MODEL slx_53ea6de5a571
CONFIG AbsTol = auto
CONFIG FixedStep = auto
CONFIG MaxStep = auto
CONFIG MinStep = auto
CONFIG RelTol = 1e-3
CONFIG SampleTimeConstraint = Unconstrained
CONFIG Solver = ode45
CONFIG SolverMode = Auto
CONFIG SolverName = ode45
CONFIG StartTime = 0.0
CONFIG StopTime = 10.0
BLOCK [Gain] D_a
  Gain = 0.0143
  OutDataTypeStr = Inherit: Inherit via internal rule
  ParamDataTypeStr = Inherit: Inherit via internal rule
  SaturateOnIntegerOverflow = off
BLOCK [Gain] D_error
  Gain = 0.05
  OutDataTypeStr = Inherit: Inherit via internal rule
  ParamDataTypeStr = Inherit: Inherit via internal rule
  SaturateOnIntegerOverflow = off
BLOCK [Derivative] Derivative
  CoefficientInTFapproximation = 1000000
BLOCK [Derivative] Derivative1
  CoefficientInTFapproximation = 1000000
BLOCK [Gain] Gear
  Gain = 6
  OutDataTypeStr = Inherit: Inherit via internal rule
  ParamDataTypeStr = Inherit: Inherit via internal rule
  SaturateOnIntegerOverflow = off
BLOCK [Gain] Gear2
  OutDataTypeStr = Inherit: Inherit via internal rule
  ParamDataTypeStr = Inherit: Inherit via internal rule
  SaturateOnIntegerOverflow = off
BLOCK [Gain] Gear3
  Gain = 6
  OutDataTypeStr = Inherit: Inherit via internal rule
  ParamDataTypeStr = Inherit: Inherit via internal rule
  SaturateOnIntegerOverflow = off
BLOCK [Gain] J_a
  Gain = 542E-7
  OutDataTypeStr = Inherit: Inherit via internal rule
  ParamDataTypeStr = Inherit: Inherit via internal rule
  SaturateOnIntegerOverflow = off
BLOCK [Gain] J_error
  Gain = 0.000001
  OutDataTypeStr = Inherit: Inherit via internal rule
  ParamDataTypeStr = Inherit: Inherit via internal rule
  SaturateOnIntegerOverflow = off
BLOCK [Gain] Kb
  Gain = 0.038506
  OutDataTypeStr = Inherit: Inherit via internal rule
  ParamDataTypeStr = Inherit: Inherit via internal rule
  SaturateOnIntegerOverflow = off
BLOCK [Gain] Kt
  Gain = 0.0385
  OutDataTypeStr = Inherit: Inherit via internal rule
  ParamDataTypeStr = Inherit: Inherit via internal rule
  SaturateOnIntegerOverflow = off
BLOCK [TransferFcn] Motor tidskonstant
  Denominator = [1 0.00378^-1]
  Numerator = [0.00378^-1]
BLOCK [Outport] Out1
  IconDisplay = Port number
BLOCK [Outport] Out2
  IconDisplay = Port number
  Port = 2
BLOCK [Reference] PID Controller  REF=simulink/Continuous/PID Controller
  AntiWindupMode = clamping
  Controller = PI
  ControllerParametersSource = internal
  D = 0
  DGainOutDataTypeStr = Inherit: Inherit via internal rule
  DOutDataTypeStr = Inherit: Inherit via internal rule
  DOutMax = []
  DOutMin = []
  DParamDataTypeStr = Inherit: Inherit via internal rule
  DParamMax = []
  DParamMin = []
  DProdOutDataTypeStr = Inherit: Inherit via internal rule
  DifferentiatorICPrevScaledInput = 0
  DifferentiatorOutDataTypeStr = Inherit: Inherit via internal rule
  DifferentiatorOutMax = []
  DifferentiatorOutMin = []
  ExternalReset = none
  FilterContinuousStateAttributes = ''
  FilterMethod = Forward Euler
  FilterOutDataTypeStr = Inherit: Inherit via internal rule
  FilterOutMax = []
  FilterOutMin = []
  FilterRTWStateStorageClass = Auto
  FilterStateMustResolveToSignalObject = off
  Form = Parallel
  I = 6000
  IGainOutDataTypeStr = Inherit: Inherit via internal rule
  IOutDataTypeStr = Inherit: Inherit via internal rule
  IOutMax = []
  IOutMin = []
  IParamDataTypeStr = Inherit: Inherit via internal rule
  IParamMax = []
  IParamMin = []
  IProdOutDataTypeStr = Inherit: Inherit via internal rule
  IgnoreLimit = off
  InitialConditionForFilter = 0
  InitialConditionForIntegrator = 0
  InitialConditionSource = internal
  IntegratorContinuousStateAttributes = ''
  IntegratorMethod = Forward Euler
  IntegratorOutDataTypeStr = Inherit: Inherit via internal rule
  IntegratorOutMax = []
  IntegratorOutMin = []
  IntegratorRTWStateStorageClass = Auto
  IntegratorStateMustResolveToSignalObject = off
  Kb = 1
  KbOutDataTypeStr = Inherit: Inherit via internal rule
  KbOutMax = []
  KbOutMin = []
  KbParamDataTypeStr = Inherit: Inherit via internal rule
  KbParamMax = []
  KbParamMin = []
  Kt = 1
  KtOutDataTypeStr = Inherit: Inherit via internal rule
  KtOutMax = []
  KtOutMin = []
  KtParamDataTypeStr = Inherit: Inherit via internal rule
  KtParamMax = []
  KtParamMin = []
  LimitOutput = on
  LinearizeAsGain = off
  LockScale = off
  LowerSaturationLimit = 0
  N = 100
  NGainOutDataTypeStr = Inherit: Inherit via internal rule
  NOutDataTypeStr = Inherit: Inherit via internal rule
  NOutMax = []
  NOutMin = []
  NParamDataTypeStr = Inherit: Inherit via internal rule
  NParamMax = []
  NParamMin = []
  NProdOutDataTypeStr = Inherit: Inherit via internal rule
  P = 5
  PGainOutDataTypeStr = Inherit: Inherit via internal rule
  POutDataTypeStr = Inherit: Inherit via internal rule
  POutMax = []
  POutMin = []
  PParamDataTypeStr = Inherit: Inherit via internal rule
  PParamMax = []
  PParamMin = []
  PProdOutDataTypeStr = Inherit: Inherit via internal rule
  Ports = [1, 1]
  RndMeth = Floor
  SampleTime = -1
  SaturateOnIntegerOverflow = off
  SaturationOutDataTypeStr = Inherit: Same as input
  SaturationOutMax = []
  SaturationOutMin = []
  SourceBlock = simulink/Continuous/PID Controller
  SourceType = PID 1dof
  SumAccumDataTypeStr = Inherit: Inherit via internal rule
  SumDAccumDataTypeStr = Inherit: Inherit via internal rule
  SumDOutDataTypeStr = Inherit: Inherit via internal rule
  SumDOutMax = []
  SumDOutMin = []
  SumI1AccumDataTypeStr = Inherit: Inherit via internal rule
  SumI1OutDataTypeStr = Inherit: Inherit via internal rule
  SumI1OutMax = []
  SumI1OutMin = []
  SumI2AccumDataTypeStr = Inherit: Inherit via internal rule
  SumI2OutDataTypeStr = Inherit: Inherit via internal rule
  SumI2OutMax = []
  SumI2OutMin = []
  SumI3AccumDataTypeStr = Inherit: Inherit via internal rule
  SumI3OutDataTypeStr = Inherit: Inherit via internal rule
  SumI3OutMax = []
  SumI3OutMin = []
  SumOutDataTypeStr = Inherit: Inherit via internal rule
  SumOutMax = []
  SumOutMin = []
  TimeDomain = Continuous-time
  TrackingMode = off
  UpperSaturationLimit = 100
  UseFilter = off
  ZeroCross = on
BLOCK [Gain] PWM->Volt
  Gain = 1/100
  OutDataTypeStr = Inherit: Inherit via internal rule
  ParamDataTypeStr = Inherit: Inherit via internal rule
  SaturateOnIntegerOverflow = off
BLOCK [Product] Product
  InputSameDT = off
  OutDataTypeStr = Inherit: Inherit via internal rule
  Ports = [2, 1]
  RndMeth = Floor
  SaturateOnIntegerOverflow = off
BLOCK [Quantizer] Quantizer
BLOCK [RateLimiter] Rate Limiter
  RisingSlewLimit = 5
BLOCK [Step] Step Hastighed
  After = 30
  SampleTime = 0
BLOCK [Sum] Sum
  IconShape = round
  InputSameDT = off
  Inputs = |+-
  OutDataTypeStr = Inherit: Inherit via internal rule
  Ports = [2, 1]
  SaturateOnIntegerOverflow = off
BLOCK [Sum] Sum1
  IconShape = round
  InputSameDT = off
  Inputs = ++|
  OutDataTypeStr = Inherit: Inherit via internal rule
  Ports = [2, 1]
  SaturateOnIntegerOverflow = off
BLOCK [Sum] Sum2
  IconShape = round
  InputSameDT = off
  Inputs = +|+
  OutDataTypeStr = Inherit: Inherit via internal rule
  Ports = [2, 1]
  SaturateOnIntegerOverflow = off
BLOCK [Sum] Sum3
  IconShape = round
  InputSameDT = off
  Inputs = +|+
  OutDataTypeStr = Inherit: Inherit via internal rule
  Ports = [2, 1]
  SaturateOnIntegerOverflow = off
BLOCK [Sum] Sum4
  IconShape = round
  InputSameDT = off
  Inputs = ++|
  OutDataTypeStr = Inherit: Inherit via internal rule
  Ports = [2, 1]
  SaturateOnIntegerOverflow = off
BLOCK [TransferFcn] Transfer Fcn
  Denominator = [0.000072 0.608]
BLOCK [TransferFcn] Transfer Fcn1
  Denominator = [1 5]
  Numerator = [5]
BLOCK [UnitDelay] Unit Delay
  InputProcessing = Elements as channels (sample based)
  SampleTime = 0.005
BLOCK [UnitDelay] Unit Delay1
  InputProcessing = Elements as channels (sample based)
  SampleTime = 0.005
BLOCK [Constant] set Moment
  Value = 1.6
BLOCK [Constant] set Moment1
  Value = 30
BLOCK [Gain] v->omega
  Gain = 2*pi/(2*pi*10)
  OutDataTypeStr = Inherit: Inherit via internal rule
  ParamDataTypeStr = Inherit: Inherit via internal rule
  SaturateOnIntegerOverflow = off
LINE D_a:1 -> Sum2:2
LINE D_error:1 -> Sum3:2
LINE Derivative1:1 -> J_error:1
LINE Derivative:1 -> J_a:1
LINE Gear2:1 -> Sum4:1
LINE Gear3:1 -> Out1:1
LINE Gear3:1 -> Sum4:2
LINE Gear3:1 -> Sum:2
LINE Gear:1 -> D_a:1
LINE Gear:1 -> Derivative:1
LINE Gear:1 -> Motor tidskonstant:1
LINE J_a:1 -> Sum2:1
LINE J_error:1 -> Sum3:1
LINE Kb:1 -> Transfer Fcn:1
LINE Kt:1 -> Sum1:2
LINE Motor tidskonstant:1 -> Kb:1
LINE PID Controller:1 -> Unit Delay1:1
LINE PWM->Volt:1 -> Product:2
LINE Product:1 -> Kt:1
LINE Quantizer:1 -> PWM->Volt:1
LINE Rate Limiter:1 -> Transfer Fcn1:1
LINE Step Hastighed:1 -> Rate Limiter:1
LINE Sum1:1 -> Gear3:1
LINE Sum2:1 -> Sum1:1
LINE Sum3:1 -> Gear2:1
LINE Sum4:1 -> Out2:1
LINE Sum:1 -> Unit Delay:1
LINE Transfer Fcn1:1 -> v->omega:1
LINE Transfer Fcn:1 -> Product:1
LINE Unit Delay1:1 -> Quantizer:1
LINE Unit Delay:1 -> PID Controller:1
LINE set Moment:1 -> Sum:1
LINE v->omega:1 -> D_error:1
LINE v->omega:1 -> Derivative1:1
LINE v->omega:1 -> Gear:1
